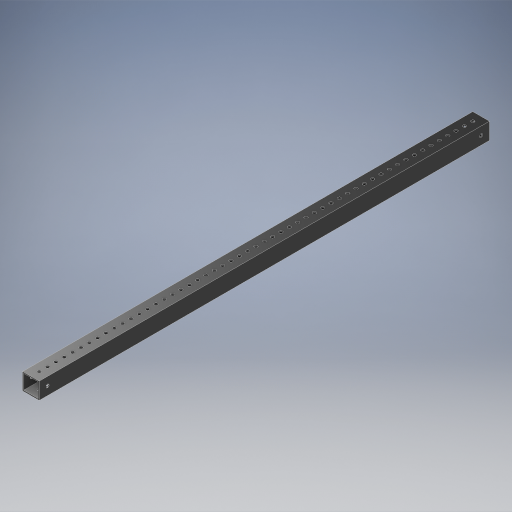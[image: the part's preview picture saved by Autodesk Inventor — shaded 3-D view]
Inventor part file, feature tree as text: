
AUTODESK INVENTOR PART (.ipt)
format: ipt  version: 2024.2 (Build 282272000, 272)  size: 870,400 bytes
history: native  units: in
note: dims shown in document units (in); Inventor stores cm internally (conversion verified against a paired STEP export)
features: other x13, extrude x9, hole x3, pattern_linear x3, mirror x3, sheet_metal_op x1, plane x1
ambient origin geometry x8: Origin, YZ Plane, XZ Plane, XY Plane, X Axis, Y Axis, Z Axis, Center Point
bodies: Solid1 (feature_tree)
feature tree (33):
  other  "Blocks"
  other  "Base Sketch"
  extrude  "Base"  Depth=1.0in
  extrude  "MAX Corner"  Depth=1.0in
  extrude  "MAX Corner Cut"  Depth=0.0625in
  extrude  "Scribe Lines"  Depth=0.0625in
  other  "Side Middle"
  other  "Top Middle"
  other  "Side Holes Sketch"
  hole  "Top Side Hole"  [1 undecoded]
  hole  "Mid Side Hole"  [1 undecoded]
  hole  "Btm Side Hole"  [1 undecoded]
  pattern_linear  "Side Holes"  Spacing1=0.04in  [1 undecoded]
  mirror  "Side Mirror"
  extrude  "MAXTube Hole"  Depth=0.04in
  extrude  "MAXTube Outside"  Depth=27.0in
  pattern_linear  "MAXTube Pattern"  Spacing1=0.0in  [1 undecoded]
  mirror  "MAXTube Mirror"
  extrude  "Left Top Hole"  Depth=27.0in
  extrude  "Mid Top Hole"  TaperAngle=0.0deg  [1 undecoded]
  extrude  "Right Top Hole"  TaperAngle=0.0deg  [1 undecoded]
  pattern_linear  "Top Holes"  Spacing1=0.005in  [1 undecoded]
  mirror  "Top Mirror"
  sheet_metal_op  "Corner"
  other  "MAXTube"
  plane  "Work Plane3"
  other  "Corner:5"
  other  "Corner:6"
  other  "Corner:7"
  other  "Corner:8"
  other  "MAXTube:1"
  other  "MAXTube:2"
  other  "MAXTube:3"
note: 8 required parameter values undecoded (feature->parameter linkage not recoverable at this tier; creation-order binding heuristic only, values carry confidence <= 0.55)
